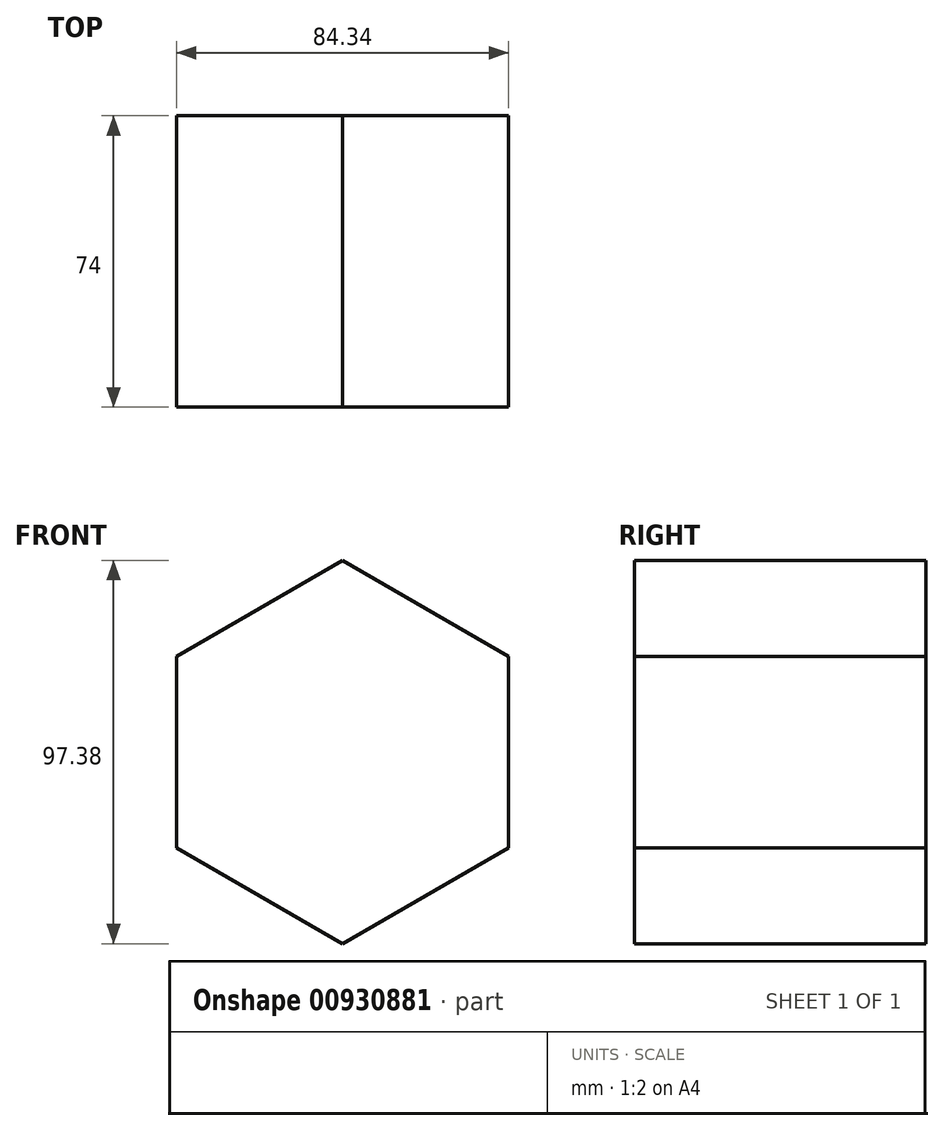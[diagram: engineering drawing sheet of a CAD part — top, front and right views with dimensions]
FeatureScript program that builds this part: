
annotation { "Feature Type Name" : "Feature", "Feature Type Description" : "" }
export const myFeature = defineFeature(function(context is Context, id is Id, definition is map)
    precondition{}
    {
        {
            var Q0;
            Q0=qCreatedBy(makeId("Front.planeOp"),FACE);
            var sketch = newSketch(context, id + "F0", { "sketchPlane" : qUnion([Q0])});
            skCircle(sketch, "E0.cCircle", {"center": v(0, 0) * mm, "radius": 42.17 * mm, "construction": true});
            skLineSegment(sketch, "E0.0", {"start": v(0, -48.69) * mm, "end": v(-42.17, -24.34) * mm});
            skLineSegment(sketch, "E0.1", {"start": v(-42.17, -24.34) * mm, "end": v(-42.17, 24.34) * mm});
            skLineSegment(sketch, "E0.2", {"start": v(-42.17, 24.34) * mm, "end": v(0, 48.69) * mm});
            skLineSegment(sketch, "E0.3", {"start": v(0, 48.69) * mm, "end": v(42.17, 24.34) * mm});
            skLineSegment(sketch, "E0.4", {"start": v(42.17, 24.34) * mm, "end": v(42.17, -24.34) * mm});
            skLineSegment(sketch, "E0.5", {"start": v(42.17, -24.34) * mm, "end": v(0, -48.69) * mm});
            skPoint(sketch, "E0.0.midPoint", {"position": v(-21.08, -36.52) * mm});
            skSolve(sketch);
        }
        {
            var Q0;
            Q0=makeQuery(id+"F0.imprint","IMPRINT",FACE,{"disambiguationData":[TD([[makeQuery(id+"F0.imprint","IMPRINT",EDGE,{"derivedFrom":sQuery(id+"F0.wireOp",EDGE,"E0.0")}),-1.0]])]});
            extrude(context, id + "F1", {"entities" : qUnion([Q0]), "depth" : 74 * mm, "offsetDistance" : 25 * mm});
        }
    });
